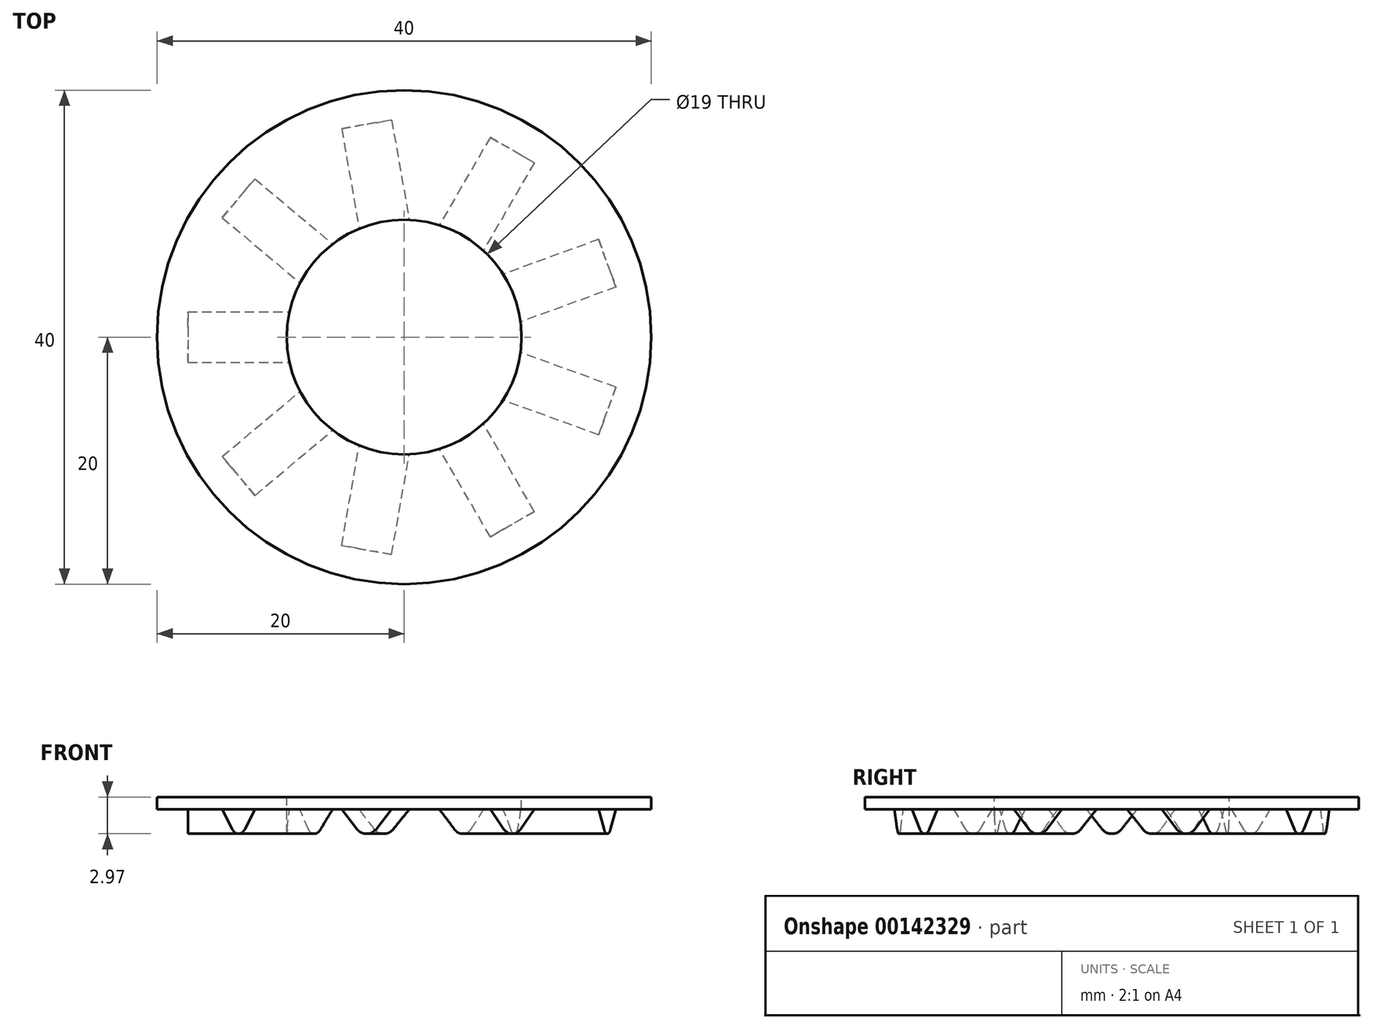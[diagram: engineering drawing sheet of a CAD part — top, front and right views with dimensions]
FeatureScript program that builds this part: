
annotation { "Feature Type Name" : "Feature", "Feature Type Description" : "" }
export const myFeature = defineFeature(function(context is Context, id is Id, definition is map)
    precondition{}
    {
        {
            var Q0;
            Q0=qCreatedBy(makeId("Top.planeOp"),FACE);
            var sketch = newSketch(context, id + "F0", { "sketchPlane" : qUnion([Q0])});
            skCircle(sketch, "E0", {"center": v(0, 0) * mm, "radius": 20 * mm});
            skCircle(sketch, "E1", {"center": v(0, 0) * mm, "radius": 9.5 * mm});
            skSolve(sketch);
        }
        {
            var Q0;
            Q0 = qSketchRegion(id + "F0", true);
            var Q1;
            Q1=makeQuery(id+"F0.imprint","IMPRINT",FACE,{"disambiguationData":[TD([[makeQuery(id+"F0.imprint","IMPRINT",EDGE,{"derivedFrom":sQuery(id+"F0.wireOp",EDGE,"E1")}),1.0]])]});
            extrude(context, id + "F1", {"entities" : qUnion([Q0, Q1]), "depth" : 1 * mm});
        }
        {
            var Q0;
            Q0=qCreatedBy(makeId("Top.planeOp"),FACE);
            var sketch = newSketch(context, id + "F2", { "sketchPlane" : qUnion([Q0])});
            skCircle(sketch, "E2", {"center": v(0, 0) * mm, "radius": 17 * mm});
            skCircle(sketch, "E3.0", {"center": v(0, 0) * mm, "radius": 19 * mm});
            skSolve(sketch);
        }
        {
            var Q0;
            Q0=makeQuery(id+"F1.opExtrude","CAP_FACE",FACE,{"disambiguationData":[OSD([sQuery(id+"F0.wireOp",EDGE,"E0")])],"isStart":true});
            var sketch = newSketch(context, id + "F3", { "sketchPlane" : qUnion([Q0])});
            skLineSegment(sketch, "E4", {"start": v(0, 0) * mm, "end": v(-12.5, 0) * mm});
            skPoint(sketch, "E5", {"position": v(-12.5, 0) * mm});
            skSolve(sketch);
        }
        {
            var Q0;
            Q0=sQuery(id+"F3.wireOp",EDGE,"E4");
            var Q1;
            Q1=sQuery(id+"F3.wireOp",VERTEX,"E5");
            cPlane(context, id + "F4", {"entities" : qUnion([Q0, Q1]), "cplaneType" : CPlaneType.LINE_POINT, "offset" : 25 * mm, "width" : 150 * mm, "height" : 150 * mm});
        }
        {
            var Q0;
            Q0=qCreatedBy(id+"F4.planeOp",FACE);
            var sketch = newSketch(context, id + "F5", { "sketchPlane" : qUnion([Q0])});
            skLineSegment(sketch, "E6", {"start": v(-2.06, 0) * mm, "end": v(2.06, 0) * mm});
            skLineSegment(sketch, "E7", {"start": v(2.06, 0) * mm, "end": v(0, -2.58) * mm});
            skLineSegment(sketch, "E8", {"start": v(0, -2.58) * mm, "end": v(-2.06, 0) * mm});
            skSolve(sketch);
        }
        {
            var Q0;
            Q0=qSketchRegion(id+"F5",true);
            extrude(context, id + "F6", {"entities" : qUnion([Q0]), "endBound" : BoundingType.SYMMETRIC, "depth" : 10 * mm});
        }
        {
            var Q0;
            Q0=makeQuery(id+"F6.opExtrude","SWEPT_BODY",BODY,{"disambiguationData":[OSD([sQuery(id+"F5.wireOp",EDGE,"E6"),sQuery(id+"F5.wireOp",EDGE,"E7"),sQuery(id+"F5.wireOp",EDGE,"E8")])]});
            var Q1;
            Q1=sQuery(id+"F2.wireOp",EDGE,"E2");
            circularPattern(context, id + "F7", {"operationType" : NewBodyOperationType.ADD, "entities" : qUnion([Q0]), "axis" : qUnion([Q1]), "angle" : 360 * degree, "instanceCount" : 9, "equalSpace" : true});
        }
        {
            var Q0;
            Q0=makeQuery(id+"F7.opPattern","COPY",EDGE,{"derivedFrom":makeQuery(id+"F6.opExtrude","SWEPT_EDGE",EDGE,{"disambiguationData":[OSD([sQuery(id+"F5.wireOp",EDGE,"E7"),sQuery(id+"F5.wireOp",EDGE,"E8")])]}),"instanceName":"17"});
            var Q1;
            Q1=makeQuery(id+"F7.opPattern","COPY",EDGE,{"derivedFrom":makeQuery(id+"F6.opExtrude","SWEPT_EDGE",EDGE,{"disambiguationData":[OSD([sQuery(id+"F5.wireOp",EDGE,"E7"),sQuery(id+"F5.wireOp",EDGE,"E8")])]}),"instanceName":"16"});
            var Q2;
            Q2=makeQuery(id+"F7.opPattern","COPY",EDGE,{"derivedFrom":makeQuery(id+"F6.opExtrude","SWEPT_EDGE",EDGE,{"disambiguationData":[OSD([sQuery(id+"F5.wireOp",EDGE,"E7"),sQuery(id+"F5.wireOp",EDGE,"E8")])]}),"instanceName":"15"});
            var Q3;
            Q3=makeQuery(id+"F7.opPattern","COPY",EDGE,{"derivedFrom":makeQuery(id+"F6.opExtrude","SWEPT_EDGE",EDGE,{"disambiguationData":[OSD([sQuery(id+"F5.wireOp",EDGE,"E7"),sQuery(id+"F5.wireOp",EDGE,"E8")])]}),"instanceName":"14"});
            var Q4;
            Q4=makeQuery(id+"F7.opPattern","COPY",EDGE,{"derivedFrom":makeQuery(id+"F6.opExtrude","SWEPT_EDGE",EDGE,{"disambiguationData":[OSD([sQuery(id+"F5.wireOp",EDGE,"E7"),sQuery(id+"F5.wireOp",EDGE,"E8")])]}),"instanceName":"13"});
            var Q5;
            Q5=makeQuery(id+"F7.opPattern","COPY",EDGE,{"derivedFrom":makeQuery(id+"F6.opExtrude","SWEPT_EDGE",EDGE,{"disambiguationData":[OSD([sQuery(id+"F5.wireOp",EDGE,"E7"),sQuery(id+"F5.wireOp",EDGE,"E8")])]}),"instanceName":"12"});
            var Q6;
            Q6=makeQuery(id+"F7.opPattern","COPY",EDGE,{"derivedFrom":makeQuery(id+"F6.opExtrude","SWEPT_EDGE",EDGE,{"disambiguationData":[OSD([sQuery(id+"F5.wireOp",EDGE,"E7"),sQuery(id+"F5.wireOp",EDGE,"E8")])]}),"instanceName":"11"});
            var Q7;
            Q7=makeQuery(id+"F7.opPattern","COPY",EDGE,{"derivedFrom":makeQuery(id+"F6.opExtrude","SWEPT_EDGE",EDGE,{"disambiguationData":[OSD([sQuery(id+"F5.wireOp",EDGE,"E7"),sQuery(id+"F5.wireOp",EDGE,"E8")])]}),"instanceName":"10"});
            var Q8;
            Q8=makeQuery(id+"F7.opPattern","COPY",EDGE,{"derivedFrom":makeQuery(id+"F6.opExtrude","SWEPT_EDGE",EDGE,{"disambiguationData":[OSD([sQuery(id+"F5.wireOp",EDGE,"E7"),sQuery(id+"F5.wireOp",EDGE,"E8")])]}),"instanceName":"9"});
            var Q9;
            Q9=makeQuery(id+"F7.opPattern","COPY",EDGE,{"derivedFrom":makeQuery(id+"F6.opExtrude","SWEPT_EDGE",EDGE,{"disambiguationData":[OSD([sQuery(id+"F5.wireOp",EDGE,"E7"),sQuery(id+"F5.wireOp",EDGE,"E8")])]}),"instanceName":"8"});
            var Q10;
            Q10=makeQuery(id+"F7.opPattern","COPY",EDGE,{"derivedFrom":makeQuery(id+"F6.opExtrude","SWEPT_EDGE",EDGE,{"disambiguationData":[OSD([sQuery(id+"F5.wireOp",EDGE,"E7"),sQuery(id+"F5.wireOp",EDGE,"E8")])]}),"instanceName":"7"});
            var Q11;
            Q11=makeQuery(id+"F7.opPattern","COPY",EDGE,{"derivedFrom":makeQuery(id+"F6.opExtrude","SWEPT_EDGE",EDGE,{"disambiguationData":[OSD([sQuery(id+"F5.wireOp",EDGE,"E7"),sQuery(id+"F5.wireOp",EDGE,"E8")])]}),"instanceName":"6"});
            var Q12;
            Q12=makeQuery(id+"F7.opPattern","COPY",EDGE,{"derivedFrom":makeQuery(id+"F6.opExtrude","SWEPT_EDGE",EDGE,{"disambiguationData":[OSD([sQuery(id+"F5.wireOp",EDGE,"E7"),sQuery(id+"F5.wireOp",EDGE,"E8")])]}),"instanceName":"5"});
            var Q13;
            Q13=makeQuery(id+"F7.opPattern","COPY",EDGE,{"derivedFrom":makeQuery(id+"F6.opExtrude","SWEPT_EDGE",EDGE,{"disambiguationData":[OSD([sQuery(id+"F5.wireOp",EDGE,"E7"),sQuery(id+"F5.wireOp",EDGE,"E8")])]}),"instanceName":"4"});
            var Q14;
            Q14=makeQuery(id+"F7.opPattern","COPY",EDGE,{"derivedFrom":makeQuery(id+"F6.opExtrude","SWEPT_EDGE",EDGE,{"disambiguationData":[OSD([sQuery(id+"F5.wireOp",EDGE,"E7"),sQuery(id+"F5.wireOp",EDGE,"E8")])]}),"instanceName":"3"});
            var Q15;
            Q15=makeQuery(id+"F7.opPattern","COPY",EDGE,{"derivedFrom":makeQuery(id+"F6.opExtrude","SWEPT_EDGE",EDGE,{"disambiguationData":[OSD([sQuery(id+"F5.wireOp",EDGE,"E7"),sQuery(id+"F5.wireOp",EDGE,"E8")])]}),"instanceName":"2"});
            var Q16;
            Q16=makeQuery(id+"F7.opPattern","COPY",EDGE,{"derivedFrom":makeQuery(id+"F6.opExtrude","SWEPT_EDGE",EDGE,{"disambiguationData":[OSD([sQuery(id+"F5.wireOp",EDGE,"E7"),sQuery(id+"F5.wireOp",EDGE,"E8")])]}),"instanceName":"1"});
            var Q17;
            Q17=makeQuery(id+"F6.opExtrude","SWEPT_EDGE",EDGE,{"disambiguationData":[OSD([sQuery(id+"F5.wireOp",EDGE,"E7"),sQuery(id+"F5.wireOp",EDGE,"E8")])]});
            fillet(context, id + "F8", {"entities" : qUnion([Q0, Q1, Q2, Q3, Q4, Q5, Q6, Q7, Q8, Q9, Q10, Q11, Q12, Q13, Q14, Q15, Q16, Q17]), "radius" : 1 * mm, "tangentPropagation" : true, "allowEdgeOverflow" : false});
        }
        {
            var Q0;
            Q0=makeQuery(id+"F0.imprint","IMPRINT",FACE,{"disambiguationData":[TD([[makeQuery(id+"F0.imprint","IMPRINT",EDGE,{"derivedFrom":sQuery(id+"F0.wireOp",EDGE,"E1")}),1.0]])]});
            extrude(context, id + "F9", {"entities" : qUnion([Q0]), "operationType" : NewBodyOperationType.REMOVE, "endBound" : BoundingType.SYMMETRIC, "oppositeDirection" : true, "depth" : 10 * mm});
        }
    });
